FCSTD DOCUMENT  (FreeCAD 1.0R39319 (Git))
Label: Robot
License: All rights reserved
LicenseURL: https://en.wikipedia.org/wiki/All_rights_reserved
objects: App::Link×5, Spreadsheet::Sheet×1, Sketcher::SketchObject×1, PartDesign::Body×1
note: 3 computed .brp shape members not serialized (recipe doc carries the construction recipe); baked Part::Feature solids carry a one-line shape summary decoded from their .brp
EXTERNAL_REF file=DisplayHolder.FCStd obj=LinkGroup
EXTERNAL_REF file=RobotBody.FCStd obj=Body002
EXTERNAL_REF file=GT2_80.FCStd obj=LinkGroup
EXTERNAL_REF file=RobotBody.FCStd obj=LinkGroup
EXTERNAL_REF file=ChessBoard.FCStd obj=LinkGroup

FEATURE [Spreadsheet::Sheet] Spreadsheet  label="SpreadSheet"
  cells = A1='BaseWidth; B1(BaseWidth)=64; D1='TopThickness; E1(TopThickness)=2; G1='TeethNum; H1(TeethNum)=64; A2='BaseRectWidth; B2(BaseRectWidth)=40; D2='TopBearingHeight; E2(TopBearingHeight)=8; G2='CenterGearShaft; H2(CenterGearShaft)=0; A3='BaseRectHeight; B3(BaseRectHeight)=28; D3='TopBearingHole; E3(TopBearingHole)=25; G3='CutAngle; H3(CutAngle)=45; A4='HoleDiamter; B4(HoleDiamter)=28; D4='TopBearingDiameter; E4(TopBearingDiameter)=37; G4='ShaftDiameter; H4(ShaftDiameter)=6; A5='ScrewHoleDiamter; B5(ScrewHoleDiamter)=4.5; D5='TopThrustBearingHeight; E5(TopThrustBearingHeight)=4; G5='ShaftLength; H5(ShaftLength)=20; A6='CenterToScrewHole; B6(CenterToScrewHole)=24.5; D6='TopThrustBearingDiameter; E6(TopThrustBearingDiameter)=47; A7='Width; B7(Width)=120; D7='TopDiameter; E7(TopDiameter)=64; G7='GripperVerticalThread; H7(GripperVerticalThread)=5; A8='Length; B8(Length)=150; D8='TopFaceWidth; E8(TopFaceWidth)=50; G8='GripperVerticalBolt; H8(GripperVerticalBolt)=8; A9='Height; B9(Height)=70; D9='TopFaceSize; E9(TopFaceSize)=200; G9='GripperCenterToFork; H9(GripperCenterToFork)=10; A10='FirstLayerDepth; B10(FirstLayerDepth)=12; D10='SecondArmHeight; E10(SecondArmHeight)=37; G10='GripperForkDiameter; H10(GripperForkDiameter)=2; A11='UpperThickness; B11(UpperThickness)=5; D11='TopFaceHeight; E11(TopFaceHeight)=42; A12='UpperHeight; B12(UpperHeight)=80; D12='TopGearHoleDiameter; E12(TopGearHoleDiameter)=54; A13='StepperCenterToScewHole; B13(StepperCenterToScewHole)=15.5; D13='SecondShaftStepperHolderHeight; E13(SecondShaftStepperHolderHeight)=5; A14='ContactBaseWidth; B14(ContactBaseWidth)=10; D14='CenterToStepper; E14(CenterToStepper)=200; A15='StepperScrewHole; B15(StepperScrewHole)=3; D15='StepperSize; E15(StepperSize)=42; A16='MainShaftScrewBase; B16(MainShaftScrewBase)=11; D16='StepperHeight; E16(StepperHeight)=20; A17='MainShaftSize; B17(MainShaftSize)=60; D17='StepperMainHole; E17(StepperMainHole)=22; A18='MainShaftHolder; B18(MainShaftHolder)=23; D18='StepperCenterToScrew; E18(StepperCenterToScrew)=15.5; A19='MainShaftScrewDepth; B19(MainShaftScrewDepth)=5; D19='CuroaHoleSize; E19(CuroaHoleSize)=40; D20='ConnectMainArmHoleSpace; E20(ConnectMainArmHoleSpace)=5; A21='ContactHeight; B21(ContactHeight)=5; D21='SecondShaftScrewHole; E21(SecondShaftScrewHole)=4; A22='FirstArmHeight; B22(FirstArmHeight)=40; D22='SecondShaftThroughHole; E22(SecondShaftThroughHole)=8; A23='FirstArmInnerDiameter; B23(FirstArmInnerDiameter)=28; D23='BottomBearingInnerDiameter; E23(BottomBearingInnerDiameter)=40; A24='FirstArmInnerSpaceDiameter; B24(FirstArmInnerSpaceDiameter)=45; D24='BottomBearingOuterDiameter; E24(BottomBearingOuterDiameter)=52; A25='OuterDiameter; B25(OuterDiameter)=90; D25='BottomBearingHeight; E25(BottomBearingHeight)=7; A26='ContactArmWith; B26(ContactArmWith)=54; A27='ContactArmLength; B27(ContactArmLength)=15; A29='UpperBearingHole; B29(UpperBearingHole)=8; A30='UpperBearingInner; B30(UpperBearingInner)=6; A31='UpperBearingInnerDepth; B31(UpperBearingInnerDepth)=1; A32='UpperBearingOuter; B32(UpperBearingOuter)=8.1; A33='UpperBearingOuterDepth; B33(UpperBearingOuterDepth)=4; A34='LowerBearingHole; B34(LowerBearingHole)=10; A35='LowerBearingInner; B35(LowerBearingInner)=13.1; A36='LowerBearingInnerDepth; B36(LowerBearingInnerDepth)=1; A37='LowerBearingOuter; B37(LowerBearingOuter)=15.1; A38='LowerBearingOuterDepth; B38(LowerBearingOuterDepth)=4; A39='CenterSpace; B39(CenterSpace)=31; A40='UpperLowerSpace; B40(UpperLowerSpace)=13; A41='FirstToSecondHoleSpace; B41(FirstToSecondHoleSpace)=13; A42='GripperLowerBearingHole; B42(GripperLowerBearingHole)=8.1; A43='GripperUpperBearingHole; B43(GripperUpperBearingHole)=8.1; A44='GripperThickness; B44(GripperThickness)=1; A45='GripperLowerHoleDiameter; B45(GripperLowerHoleDiameter)=5; A46='GripperWidth; B46(GripperWidth)=44; A47='ThirdArmWidth; B47(ThirdArmWidth)=50; A48='ThirdArmLength; B48(ThirdArmLength)=100
FEATURE [App::Link] Link010  label="DisplayGroup"
  LinkPlacement = pos=(-57.6,-1.23143e-05,160.9) rot=(0,0,1;0rad)
  LinkedObject = -> <external DisplayHolder.FCStd>#LinkGroup
  Placement = pos=(-57.6,-1.23143e-05,160.9) rot=(0,0,1;0rad)
FEATURE [App::Link] Link011  label="BodyHolder001"
  LinkedObject = -> <external RobotBody.FCStd>#Body002
FEATURE [App::Link] Link012  label="SecondShaft"
  LinkPlacement = pos=(224.007,129.319,49) rot=(0,0,1;3.66519rad)
  LinkedObject = -> <external GT2_80.FCStd>#LinkGroup
  Placement = pos=(224.007,129.319,49) rot=(0,0,1;3.66519rad)
FEATURE [App::Link] Link013  label="RobotBody"
  LinkedObject = -> <external RobotBody.FCStd>#LinkGroup
FEATURE [App::Link] Link014  label="WoodenChessBoard"
  LinkPlacement = pos=(-58,223.8,-82.5) rot=(0,0,1;3.14159rad)
  LinkedObject = -> <external ChessBoard.FCStd>#LinkGroup
  Placement = pos=(-58,223.8,-82.5) rot=(0,0,1;3.14159rad)
FEATURE [Sketcher::SketchObject] Sketch
  ArcFitTolerance = 1e-06
  AttachmentSupport = -> [XY_Plane]
  FullyConstrained = true
  MakeInternals = false
  MapMode = 5
  sketch-geometry (2):
    g0: LineSegment StartX=0 StartY=0 StartZ=0 EndX=0 EndY=38.08 EndZ=0
    g1: LineSegment StartX=0 StartY=38.08 StartZ=0 EndX=-74.12 EndY=38.08 EndZ=0
  constraints (6):
    c: Coincident(g0,g-1)
    c: PointOnObject(g0,g-2)
    c: Coincident(g1,g0)
    c: Horizontal(g1)
    c: DistanceX(g1,g1) = 74.12
    c: DistanceY(g0,g0) = 38.08
FEATURE [PartDesign::Body] Body
  AllowCompound = false
  Group = -> [Sketch]
  Origin = -> Origin
  Placement = pos=(-0.1,-0.1,0) rot=(0,0,1;4.71239rad)

RESOLVED EXTERNAL PARTS (link-assembly join: the EXTERNAL_REF files above that resolve inside this repo's crawl, each included once):
---- part ChessBoard.FCStd = doc fcstd_d606b7bc8795 ----
FCSTD DOCUMENT  (FreeCAD 1.0R39319 (Git))
Label: ChessBoard
License: All rights reserved
LicenseURL: https://en.wikipedia.org/wiki/All_rights_reserved
objects: Sketcher::SketchObject×19, PartDesign::Pocket×10, PartDesign::Pad×8, PartDesign::Body×6, App::LinkGroup×3, App::Link×3, PartDesign::Hole×2, Part::Mirroring×2, Image::ImagePlane×1
note: 106 computed .brp shape members not serialized (recipe doc carries the construction recipe); baked Part::Feature solids carry a one-line shape summary decoded from their .brp
EXTERNAL_REF file=NavigationBoard.FCStd obj=LinkGroup
EXTERNAL_REF file=SnapLock.FCStd obj=LinkGroup
EXTERNAL_REF file=SnapLock.FCStd obj=LinkGroup001

FEATURE [Sketcher::SketchObject] Sketch
  ArcFitTolerance = 1e-06
  AttachmentSupport = -> [XY_Plane]
  FullyConstrained = true
  MakeInternals = false
  MapMode = 5
  sketch-geometry (5):
    g0: LineSegment StartX=-250 StartY=-150 StartZ=0 EndX=250 EndY=-150 EndZ=0
    g1: LineSegment StartX=250 StartY=-150 StartZ=0 EndX=250 EndY=150 EndZ=0
    g2: LineSegment StartX=250 StartY=150 StartZ=0 EndX=-250 EndY=150 EndZ=0
    g3: LineSegment StartX=-250 StartY=150 StartZ=0 EndX=-250 EndY=-150 EndZ=0
    g4: GeomPoint [constr] X=0 Y=0 Z=0
  constraints (12):
    c: Coincident(g0,g1)
    c: Coincident(g1,g2)
    c: Coincident(g2,g3)
    c: Coincident(g3,g0)
    c: Horizontal(g0)
    c: Horizontal(g2)
    c: Vertical(g1)
    c: Vertical(g3)
    c: Symmetric(g2,g0,g4)
    c: Distance(g1,g3) = 500
    c: Distance(g0,g2) = 300
    c: Coincident(g4,g-1)
FEATURE [Image::ImagePlane] ChessBoard
  Placement = pos=(0,0,30) rot=(0,0,1;0rad)
  XSize = 500.127
  YSize = 300.144
FEATURE [PartDesign::Pad] Pad
  Direction = (0,0,1)
  Length = 5
  Length2 = 10
  Profile = -> Sketch
  ReferenceAxis = -> Sketch [N_Axis]
  Refine = true
  Suppressed = false
  Type = 0
FEATURE [Sketcher::SketchObject] Sketch001
  ArcFitTolerance = 1e-06
  AttachmentSupport = -> [XY_Plane001]
  FullyConstrained = true
  MakeInternals = false
  MapMode = 5
  sketch-geometry (5):
    g0: LineSegment StartX=-150 StartY=-150 StartZ=0 EndX=150 EndY=-150 EndZ=0
    g1: LineSegment StartX=150 StartY=-150 StartZ=0 EndX=150 EndY=150 EndZ=0
    g2: LineSegment StartX=150 StartY=150 StartZ=0 EndX=-150 EndY=150 EndZ=0
    g3: LineSegment StartX=-150 StartY=150 StartZ=0 EndX=-150 EndY=-150 EndZ=0
    g4: GeomPoint [constr] X=0 Y=0 Z=0
  constraints (12):
    c: Coincident(g0,g1)
    c: Coincident(g1,g2)
    c: Coincident(g2,g3)
    c: Coincident(g3,g0)
    c: Horizontal(g0)
    c: Horizontal(g2)
    c: Vertical(g1)
    c: Vertical(g3)
    c: Symmetric(g2,g0,g4)
    c: Distance(g1,g3) = 300
    c: Distance(g0,g2) = 300
    c: Coincident(g4,g-1)
FEATURE [PartDesign::Pad] Pad001
  Direction = (0,0,1)
  Length = 5
  Length2 = 10
  Profile = -> Sketch001
  ReferenceAxis = -> Sketch001 [N_Axis]
  Refine = true
  Suppressed = false
  Type = 0
FEATURE [PartDesign::Body] Body001  label="MainBoard"
  AllowCompound = false
  Group = -> [Sketch001,Pad001]
  Origin = -> Origin001
  Placement = pos=(0,0,25) rot=(0,0,1;0rad)
  Tip = -> Pad001
FEATURE [Sketcher::SketchObject] Sketch002
  ArcFitTolerance = 1e-06
  AttachmentSupport = -> [XY_Plane002]
  FullyConstrained = true
  MakeInternals = false
  MapMode = 5
  sketch-geometry (4):
    g0: LineSegment StartX=0 StartY=0 StartZ=0 EndX=0 EndY=-300 EndZ=0
    g1: LineSegment StartX=0 StartY=-300 StartZ=0 EndX=100 EndY=-300 EndZ=0
    g2: LineSegment StartX=100 StartY=-300 StartZ=0 EndX=100 EndY=0 EndZ=0
    g3: LineSegment StartX=100 StartY=0 StartZ=0 EndX=0 EndY=0 EndZ=0
  constraints (11):
    c: Coincident(g0,g1)
    c: Coincident(g1,g2)
    c: Coincident(g2,g3)
    c: Coincident(g3,g0)
    c: Vertical(g0)
    c: Vertical(g2)
    c: Horizontal(g1)
    c: Horizontal(g3)
    c: Distance(g0,g2) = 100
    c: Distance(g1,g3) = 300
    c: Coincident(g0,g-1)
FEATURE [PartDesign::Pad] Pad002
  Direction = (0,0,1)
  Length = 5
  Length2 = 10
  Profile = -> Sketch002
  ReferenceAxis = -> Sketch002 [N_Axis]
  Refine = true
  Suppressed = false
  Type = 0
FEATURE [PartDesign::Body] Body002  label="DropLeft"
  AllowCompound = false
  Group = -> [Sketch002,Pad002]
  Origin = -> Origin002
  Placement = pos=(-250,150,25) rot=(0,0,1;0rad)
  Tip = -> Pad002
FEATURE [Sketcher::SketchObject] Sketch003
  ArcFitTolerance = 1e-06
  AttachmentSupport = -> [XY_Plane003]
  FullyConstrained = true
  MakeInternals = false
  MapMode = 5
  sketch-geometry (4):
    g0: LineSegment StartX=0 StartY=0 StartZ=0 EndX=-100 EndY=0 EndZ=0
    g1: LineSegment StartX=-100 StartY=0 StartZ=0 EndX=-100 EndY=-300 EndZ=0
    g2: LineSegment StartX=-100 StartY=-300 StartZ=0 EndX=0 EndY=-300 EndZ=0
    g3: LineSegment StartX=0 StartY=-300 StartZ=0 EndX=0 EndY=0 EndZ=0
  constraints (11):
    c: Coincident(g0,g1)
    c: Coincident(g1,g2)
    c: Coincident(g2,g3)
    c: Coincident(g3,g0)
    c: Horizontal(g0)
    c: Horizontal(g2)
    c: Vertical(g1)
    c: Vertical(g3)
    c: Distance(g1,g3) = 100
    c: Distance(g0,g2) = 300
    c: Coincident(g0,g-1)
FEATURE [PartDesign::Pad] Pad003
  Direction = (0,0,1)
  Length = 5
  Length2 = 10
  Profile = -> Sketch003
  ReferenceAxis = -> Sketch003 [N_Axis]
  Refine = true
  Suppressed = false
  Type = 0
FEATURE [PartDesign::Body] Body003  label="DropRight"
  AllowCompound = false
  Group = -> [Sketch003,Pad003]
  Origin = -> Origin003
  Placement = pos=(250,150,25) rot=(0,0,1;0rad)
  Tip = -> Pad003
FEATURE [Sketcher::SketchObject] Sketch004
  ArcFitTolerance = 1e-06
  AttachmentSupport = -> [XY_Plane004]
  FullyConstrained = false
  MakeInternals = false
  MapMode = 5
  sketch-geometry (13):
    g0: LineSegment StartX=0 StartY=40 StartZ=0 EndX=0 EndY=0 EndZ=0
    g1: LineSegment StartX=0 StartY=0 StartZ=0 EndX=160 EndY=0 EndZ=0
    g2: LineSegment StartX=0 StartY=40 StartZ=0 EndX=10 EndY=40 EndZ=0
    g3: LineSegment StartX=10 StartY=40 StartZ=0 EndX=10 EndY=30 EndZ=0
    g4: ArcOfCircle CenterX=30 CenterY=30 CenterZ=0 NormalX=0 NormalY=0 NormalZ=1 AngleXU=0 Radius=20 StartAngle=3.14159 EndAngle=4.71239
    g5: LineSegment StartX=90 StartY=42.0946 StartZ=0 EndX=115 EndY=42.0946 EndZ=0
    g6: LineSegment StartX=115 StartY=42.0946 StartZ=0 EndX=115 EndY=25 EndZ=0
    g7: LineSegment StartX=90 StartY=42.0946 StartZ=0 EndX=90 EndY=20 EndZ=0
    g8: LineSegment StartX=30 StartY=10 StartZ=0 EndX=80 EndY=10 EndZ=0
    g9: ArcOfCircle CenterX=125 CenterY=25 CenterZ=0 NormalX=0 NormalY=0 NormalZ=1 AngleXU=0 Radius=10 StartAngle=3.14159 EndAngle=4.71239
    g10: ArcOfCircle CenterX=80 CenterY=20 CenterZ=0 NormalX=0 NormalY=0 NormalZ=1 AngleXU=0 Radius=10 StartAngle=4.71239 EndAngle=6.28319
    g11: LineSegment StartX=125 StartY=15 StartZ=0 EndX=160 EndY=15 EndZ=0
    g12: LineSegment StartX=160 StartY=15 StartZ=0 EndX=160 EndY=0 EndZ=0
  constraints (38):
    c: PointOnObject(g0,g-2)
    c: Coincident(g0,g-1)
    c: Coincident(g0,g1)
    c: Coincident(g0,g2)
    c: Horizontal(g2)
    c: Coincident(g2,g3)
    c: Vertical(g3)
    c: Coincident(g4,g3)
    c: Vertical(g4,g4)
    c: Horizontal(g4,g3)
    c: Radius(g4) = 20
    c: DistanceY(g1,g9) = 15
    c: Distance(g2,g2) = 10
    c: DistanceY(g0,g0) = 40
    c: Horizontal(g5)
    c: Coincident(g5,g6)
    c: Vertical(g6)
    c: Coincident(g5,g7)
    c: Vertical(g7)
    c: Tangent(g4,g8) = -1.5708
    c: Coincident(g9,g6)
    c: Coincident(g10,g7)
    c: Coincident(g10,g8)
    c: Distance(g1,g8) = 10
    c: Radius(g10) = 10
    c: Vertical(g10,g8)
    c: Horizontal(g10,g7)
    c: Radius(g9) = 10
    c: Vertical(g9,g9)
    c: Horizontal(g9,g6)
    c: DistanceX(g-1,g10) = 80
    c: Tangent(g9,g11) = -1.5708
    c: Coincident(g11,g12)
    c: Vertical(g12)
    c: Coincident(g1,g12)
    c: Horizontal(g1)
    c: Distance(g-2,g12) = 160
    c: DistanceX(g5,g5) = 25
FEATURE [PartDesign::Pad] Pad004
  Direction = (0,0,1)
  Length = 29
  Length2 = 10
  Profile = -> Sketch004
  ReferenceAxis = -> Sketch004 [N_Axis]
  Refine = true
  Suppressed = false
  Type = 0
FEATURE [App::LinkGroup] LinkGroup002  label="TopBoard"
  ElementList = -> [Body001,Body002,Body003,ChessBoard]
  LinkMode = 0
  Placement = pos=(0,0,-1) rot=(0,0,1;0rad)
FEATURE [Sketcher::SketchObject] Sketch005
  ArcFitTolerance = 1e-06
  AttachmentSupport = -> [Pad]
  ExternalGeometry = -> [Sketch]
  FullyConstrained = false
  MakeInternals = false
  MapMode = 5
  Placement = pos=(0,0,0) rot=(1,0,0;3.14159rad)
  sketch-geometry (4):
    g0: LineSegment StartX=-92 StartY=-50 StartZ=0 EndX=-92 EndY=-193.39 EndZ=0
    g1: LineSegment StartX=-92 StartY=-193.39 StartZ=0 EndX=92 EndY=-193.39 EndZ=0
    g2: LineSegment StartX=92 StartY=-193.39 StartZ=0 EndX=92 EndY=-50 EndZ=0
    g3: LineSegment StartX=92 StartY=-50 StartZ=0 EndX=-92 EndY=-50 EndZ=0
  constraints (11):
    c: Coincident(g0,g1)
    c: Coincident(g1,g2)
    c: Coincident(g2,g3)
    c: Coincident(g3,g0)
    c: Vertical(g0)
    c: Vertical(g2)
    c: Horizontal(g1)
    c: Horizontal(g3)
    c: Distance(g-2,g2) = 92
    c: Distance(g-2,g0) = 92
    c: Distance(g-3,g3) = 100
FEATURE [PartDesign::Pocket] Pocket
  BaseFeature = -> Pad
  Direction = (0,0,1)
  Length = 5
  Length2 = 5
  Profile = -> Sketch005
  ReferenceAxis = -> Sketch005 [N_Axis]
  Refine = true
  Suppressed = false
  Type = 0
FEATURE [PartDesign::Body] Body  label="Bottom"
  AllowCompound = false
  Group = -> [Sketch,Pad,Sketch005,Pocket]
  Origin = -> Origin
  Tip = -> Pocket
FEATURE [Sketcher::SketchObject] Sketch006
  ArcFitTolerance = 1e-06
  AttachmentSupport = -> [Pad004]
  FullyConstrained = false
  MakeInternals = false
  MapMode = 5
  Placement = pos=(0,0,29) rot=(0,0,1;0rad)
  sketch-geometry (6):
    g0: LineSegment StartX=5 StartY=45 StartZ=0 EndX=5 EndY=5 EndZ=0
    g1: LineSegment StartX=5 StartY=5 StartZ=0 EndX=100 EndY=5 EndZ=0
    g2: LineSegment StartX=275.375 StartY=45 StartZ=0 EndX=5 EndY=45 EndZ=0
    g3: LineSegment StartX=100 StartY=5 StartZ=0 EndX=100 EndY=-8.02974 EndZ=0
    g4: LineSegment StartX=100 StartY=-8.02974 StartZ=0 EndX=275.375 EndY=-8.02974 EndZ=0
    g5: LineSegment StartX=275.375 StartY=45 StartZ=0 EndX=275.375 EndY=-8.02974 EndZ=0
  constraints (16):
    c: Coincident(g0,g1)
    c: Coincident(g2,g0)
    c: Vertical(g0)
    c: Horizontal(g1)
    c: Horizontal(g2)
    c: Distance(g-2,g0) = 5
    c: Distance(g-1,g1) = 5
    c: DistanceY(g0,g0) = 40
    c: Vertical(g3)
    c: Coincident(g3,g4)
    c: Horizontal(g4)
    c: Coincident(g1,g3)
    c: Coincident(g5,g2)
    c: Coincident(g5,g4)
    c: Vertical(g5)
    c: Distance(g-2,g3) = 100
FEATURE [PartDesign::Pocket] Pocket001
  BaseFeature = -> Pad004
  Direction = (0,0,-1)
  Length = 5
  Length2 = 5
  Profile = -> Sketch006
  ReferenceAxis = -> Sketch006 [N_Axis]
  Refine = true
  Suppressed = false
  Type = 0
FEATURE [Sketcher::SketchObject] Sketch007
  ArcFitTolerance = 1e-06
  AttachmentSupport = -> [Pocket001]
  FullyConstrained = false
  MakeInternals = false
  MapMode = 5
  Placement = pos=(0,0,0) rot=(1,0,0;3.14159rad)
  sketch-geometry (6):
    g0: LineSegment StartX=5 StartY=-5 StartZ=0 EndX=5 EndY=-45 EndZ=0
    g1: LineSegment StartX=5 StartY=-45 StartZ=0 EndX=160 EndY=-45 EndZ=0
    g2: LineSegment StartX=45 StartY=-5 StartZ=0 EndX=5 EndY=-5 EndZ=0
    g3: LineSegment StartX=45 StartY=-5 StartZ=0 EndX=45 EndY=8.54607 EndZ=0
    g4: LineSegment StartX=45 StartY=8.54607 StartZ=0 EndX=160 EndY=8.54607 EndZ=0
    g5: LineSegment StartX=160 StartY=8.54607 StartZ=0 EndX=160 EndY=-45 EndZ=0
  constraints (17):
    c: Coincident(g0,g1)
    c: Coincident(g2,g0)
    c: Vertical(g0)
    c: Horizontal(g1)
    c: Horizontal(g2)
    c: Distance(g-1,g2) = 5
    c: Distance(g-2,g0) = 5
    c: DistanceY(g0,g0) = 40
    c: Coincident(g2,g3)
    c: Vertical(g3)
    c: Coincident(g3,g4)
    c: Horizontal(g4)
    c: Coincident(g4,g5)
    c: Coincident(g5,g1)
    c: Vertical(g5)
    c: DistanceX(g0,g2) = 40
    c: Distance(g1,g-2) = 160
FEATURE [PartDesign::Pocket] Pocket002
  BaseFeature = -> Pocket001
  Direction = (0,0,1)
  Length = 5
  Length2 = 5
  Profile = -> Sketch007
  ReferenceAxis = -> Sketch007 [N_Axis]
  Refine = true
  Suppressed = false
  Type = 0
FEATURE [Sketcher::SketchObject] Sketch008
  ArcFitTolerance = 1e-06
  AttachmentSupport = -> [Pocket002]
  ExternalGeometry = -> [Pocket002]
  FullyConstrained = true
  MakeInternals = false
  MapMode = 5
  Placement = pos=(0,0,24) rot=(0,0,1;0rad)
  sketch-geometry (1):
    g0: Circle CenterX=110 CenterY=10 CenterZ=0 NormalX=0 NormalY=0 NormalZ=1 AngleXU=0 Radius=5
  constraints (3):
    c: Diameter(g0) = 10
    c: Distance(g0,g-1) = 10
    c: DistanceX(g-3,g0) = 10
FEATURE [PartDesign::Pocket] Pocket003
  BaseFeature = -> Pocket002
  Direction = (0,0,-1)
  Length = 10
  Length2 = 5
  Profile = -> Sketch008
  ReferenceAxis = -> Sketch008 [N_Axis]
  Refine = true
  Suppressed = false
  Type = 0
FEATURE [Sketcher::SketchObject] Sketch009
  ArcFitTolerance = 1e-06
  AttachmentSupport = -> [XY_Plane005]
  FullyConstrained = false
  MakeInternals = false
  MapMode = 5
  sketch-geometry (13):
    g0: LineSegment StartX=0 StartY=40 StartZ=0 EndX=0 EndY=0 EndZ=0
    g1: LineSegment StartX=0 StartY=0 StartZ=0 EndX=160 EndY=0 EndZ=0
    g2: LineSegment StartX=0 StartY=40 StartZ=0 EndX=10 EndY=40 EndZ=0
    g3: LineSegment StartX=10 StartY=40 StartZ=0 EndX=10 EndY=30 EndZ=0
    g4: ArcOfCircle CenterX=30 CenterY=30 CenterZ=0 NormalX=0 NormalY=0 NormalZ=1 AngleXU=0 Radius=20 StartAngle=3.14159 EndAngle=4.71239
    g5: LineSegment StartX=90 StartY=42.0946 StartZ=0 EndX=115 EndY=42.0946 EndZ=0
    g6: LineSegment StartX=115 StartY=42.0946 StartZ=0 EndX=115 EndY=25 EndZ=0
    g7: LineSegment StartX=90 StartY=42.0946 StartZ=0 EndX=90 EndY=20 EndZ=0
    g8: LineSegment StartX=30 StartY=10 StartZ=0 EndX=80 EndY=10 EndZ=0
    g9: ArcOfCircle CenterX=125 CenterY=25 CenterZ=0 NormalX=0 NormalY=0 NormalZ=1 AngleXU=0 Radius=10 StartAngle=3.14159 EndAngle=4.71239
    g10: ArcOfCircle CenterX=80 CenterY=20 CenterZ=0 NormalX=0 NormalY=0 NormalZ=1 AngleXU=0 Radius=10 StartAngle=4.71239 EndAngle=6.28319
    g11: LineSegment StartX=125 StartY=15 StartZ=0 EndX=160 EndY=15 EndZ=0
    g12: LineSegment StartX=160 StartY=15 StartZ=0 EndX=160 EndY=0 EndZ=0
  constraints (38):
    c: PointOnObject(g0,g-2)
    c: Coincident(g0,g-1)
    c: Coincident(g0,g1)
    c: Coincident(g0,g2)
    c: Horizontal(g2)
    c: Coincident(g2,g3)
    c: Vertical(g3)
    c: Coincident(g4,g3)
    c: Vertical(g4,g4)
    c: Horizontal(g4,g3)
    c: Radius(g4) = 20
    c: DistanceY(g1,g9) = 15
    c: Distance(g2,g2) = 10
    c: DistanceY(g0,g0) = 40
    c: Horizontal(g5)
    c: Coincident(g5,g6)
    c: Vertical(g6)
    c: Coincident(g5,g7)
    c: Vertical(g7)
    c: Tangent(g4,g8) = -1.5708
    c: Coincident(g9,g6)
    c: Coincident(g10,g7)
    c: Coincident(g10,g8)
    c: Distance(g1,g8) = 10
    c: Radius(g10) = 10
    c: Vertical(g10,g8)
    c: Horizontal(g10,g7)
    c: Radius(g9) = 10
    c: Vertical(g9,g9)
    c: Horizontal(g9,g6)
    c: DistanceX(g-1,g10) = 80
    c: Tangent(g9,g11) = -1.5708
    c: Coincident(g11,g12)
    c: Vertical(g12)
    c: Coincident(g1,g12)
    c: Horizontal(g1)
    c: Distance(g-2,g12) = 160
    c: DistanceX(g5,g5) = 25
FEATURE [PartDesign::Pad] Pad005
  Direction = (0,0,1)
  Length = 29
  Length2 = 10
  Profile = -> Sketch009
  ReferenceAxis = -> Sketch009 [N_Axis]
  Refine = true
  Suppressed = false
  Type = 0
FEATURE [Sketcher::SketchObject] Sketch010
  ArcFitTolerance = 1e-06
  AttachmentSupport = -> [Pad005]
  FullyConstrained = false
  MakeInternals = false
  MapMode = 5
  Placement = pos=(0,0,29) rot=(0,0,1;0rad)
  sketch-geometry (6):
    g0: LineSegment StartX=5 StartY=45 StartZ=0 EndX=5 EndY=5 EndZ=0
    g1: LineSegment StartX=5 StartY=5 StartZ=0 EndX=100 EndY=5 EndZ=0
    g2: LineSegment StartX=275.375 StartY=45 StartZ=0 EndX=5 EndY=45 EndZ=0
    g3: LineSegment StartX=100 StartY=5 StartZ=0 EndX=100 EndY=-8.02974 EndZ=0
    g4: LineSegment StartX=100 StartY=-8.02974 StartZ=0 EndX=275.375 EndY=-8.02974 EndZ=0
    g5: LineSegment StartX=275.375 StartY=45 StartZ=0 EndX=275.375 EndY=-8.02974 EndZ=0
  constraints (16):
    c: Coincident(g0,g1)
    c: Coincident(g2,g0)
    c: Vertical(g0)
    c: Horizontal(g1)
    c: Horizontal(g2)
    c: Distance(g-2,g0) = 5
    c: Distance(g-1,g1) = 5
    c: DistanceY(g0,g0) = 40
    c: Vertical(g3)
    c: Coincident(g3,g4)
    c: Horizontal(g4)
    c: Coincident(g1,g3)
    c: Coincident(g5,g2)
    c: Coincident(g5,g4)
    c: Vertical(g5)
    c: Distance(g-2,g3) = 100
FEATURE [PartDesign::Pocket] Pocket004
  BaseFeature = -> Pad005
  Direction = (0,0,-1)
  Length = 5
  Length2 = 5
  Profile = -> Sketch010
  ReferenceAxis = -> Sketch010 [N_Axis]
  Refine = true
  Suppressed = false
  Type = 0
FEATURE [Sketcher::SketchObject] Sketch011
  ArcFitTolerance = 1e-06
  AttachmentSupport = -> [Pocket004]
  FullyConstrained = false
  MakeInternals = false
  MapMode = 5
  Placement = pos=(0,0,0) rot=(1,0,0;3.14159rad)
  sketch-geometry (6):
    g0: LineSegment StartX=5 StartY=-5 StartZ=0 EndX=5 EndY=-45 EndZ=0
    g1: LineSegment StartX=5 StartY=-45 StartZ=0 EndX=160 EndY=-45 EndZ=0
    g2: LineSegment StartX=45 StartY=-5 StartZ=0 EndX=5 EndY=-5 EndZ=0
    g3: LineSegment StartX=45 StartY=-5 StartZ=0 EndX=45 EndY=8.54607 EndZ=0
    g4: LineSegment StartX=45 StartY=8.54607 StartZ=0 EndX=160 EndY=8.54607 EndZ=0
    g5: LineSegment StartX=160 StartY=8.54607 StartZ=0 EndX=160 EndY=-45 EndZ=0
  constraints (17):
    c: Coincident(g0,g1)
    c: Coincident(g2,g0)
    c: Vertical(g0)
    c: Horizontal(g1)
    c: Horizontal(g2)
    c: Distance(g-1,g2) = 5
    c: Distance(g-2,g0) = 5
    c: DistanceY(g0,g0) = 40
    c: Coincident(g2,g3)
    c: Vertical(g3)
    c: Coincident(g3,g4)
    c: Horizontal(g4)
    c: Coincident(g4,g5)
    c: Coincident(g5,g1)
    c: Vertical(g5)
    c: DistanceX(g0,g2) = 40
    c: Distance(g1,g-2) = 160
FEATURE [PartDesign::Pocket] Pocket005
  BaseFeature = -> Pocket004
  Direction = (0,0,1)
  Length = 5
  Length2 = 5
  Profile = -> Sketch011
  ReferenceAxis = -> Sketch011 [N_Axis]
  Refine = true
  Suppressed = false
  Type = 0
FEATURE [Sketcher::SketchObject] Sketch012
  ArcFitTolerance = 1e-06
  AttachmentSupport = -> [Pocket005]
  ExternalGeometry = -> [Pocket005]
  FullyConstrained = true
  MakeInternals = false
  MapMode = 5
  Placement = pos=(0,0,24) rot=(0,0,1;0rad)
  sketch-geometry (1):
    g0: Circle CenterX=110 CenterY=10 CenterZ=0 NormalX=0 NormalY=0 NormalZ=1 AngleXU=0 Radius=5
  constraints (3):
    c: Diameter(g0) = 10
    c: Distance(g0,g-1) = 10
    c: DistanceX(g-3,g0) = 10
FEATURE [PartDesign::Pocket] Pocket006
  BaseFeature = -> Pocket005
  Direction = (0,0,-1)
  Length = 10
  Length2 = 5
  Profile = -> Sketch012
  ReferenceAxis = -> Sketch012 [N_Axis]
  Refine = true
  Suppressed = false
  Type = 0
FEATURE [Sketcher::SketchObject] Sketch013
  ArcFitTolerance = 1e-06
  AttachmentSupport = -> [Pocket006]
  ExternalGeometry = -> [Pocket006]
  FullyConstrained = true
  MakeInternals = false
  MapMode = 5
  Placement = pos=(160,0,0) rot=(0.57735,0.57735,0.57735;2.0944rad)
  sketch-geometry (4):
    g0: LineSegment StartX=15 StartY=24 StartZ=0 EndX=0 EndY=24 EndZ=0
    g1: LineSegment StartX=0 StartY=24 StartZ=0 EndX=0 EndY=15 EndZ=0
    g2: LineSegment StartX=0 StartY=15 StartZ=0 EndX=15 EndY=15 EndZ=0
    g3: LineSegment StartX=15 StartY=15 StartZ=0 EndX=15 EndY=24 EndZ=0
  constraints (11):
    c: Coincident(g0,g1)
    c: Coincident(g1,g2)
    c: Coincident(g2,g3)
    c: Coincident(g3,g0)
    c: Horizontal(g0)
    c: Horizontal(g2)
    c: Vertical(g1)
    c: Vertical(g3)
    c: Coincident(g0,g-3)
    c: PointOnObject(g1,g-2)
    c: Distance(g-1,g2) = 15
FEATURE [PartDesign::Pad] Pad006
  BaseFeature = -> Pocket006
  Direction = (1,0,0)
  Length = 15
  Length2 = 10
  Profile = -> Sketch013
  ReferenceAxis = -> Sketch013 [N_Axis]
  Refine = true
  Suppressed = false
  Type = 0
FEATURE [Sketcher::SketchObject] Sketch014
  ArcFitTolerance = 1e-06
  AttachmentSupport = -> [Pad006]
  ExternalGeometry = -> [Pad006]
  FullyConstrained = true
  MakeInternals = false
  MapMode = 5
  Placement = pos=(0,0,24) rot=(0,0,1;0rad)
  sketch-geometry (1):
    g0: Circle CenterX=167.5 CenterY=7.5 CenterZ=0 NormalX=0 NormalY=0 NormalZ=1 AngleXU=0 Radius=1.75
  constraints (2):
    c: Diameter(g0) = 3.5
    c: Symmetric(g-3,g-4,g0)
FEATURE [PartDesign::Hole] Hole
  BaseFeature = -> Pad006
  CustomThreadClearance = 0
  Depth = 25
  DepthType = 0
  Diameter = 3
  DrillForDepth = false
  DrillPoint = 1
  DrillPointAngle = 118
  HoleCutCountersinkAngle = 90
  HoleCutCustomValues = false
  HoleCutDepth = 0
  HoleCutDiameter = 6.1
  HoleCutType = 0
  ModelThread = false
  Profile = -> Sketch014
  Refine = true
  Suppressed = false
  Tapered = false
  TaperedAngle = 90
  ThreadClass = 0
  ThreadDepth = 25
  ThreadDepthType = 0
  ThreadDirection = 0
  ThreadFit = 0
  ThreadSize = 0
  ThreadType = 0
  Threaded = false
  UseCustomThreadClearance = false
FEATURE [PartDesign::Hole] Hole001
  BaseFeature = -> Hole
  CustomThreadClearance = 0
  Depth = 6
  DepthType = 0
  Diameter = 8
  DrillForDepth = false
  DrillPoint = 0
  DrillPointAngle = 118
  HoleCutCountersinkAngle = 90
  HoleCutCustomValues = false
  HoleCutDepth = 0
  HoleCutDiameter = 6.1
  HoleCutType = 0
  ModelThread = false
  Profile = -> Sketch014
  Refine = true
  Suppressed = false
  Tapered = false
  TaperedAngle = 90
  ThreadClass = 0
  ThreadDepth = 6
  ThreadDepthType = 0
  ThreadDirection = 0
  ThreadFit = 0
  ThreadSize = 0
  ThreadType = 0
  Threaded = false
  UseCustomThreadClearance = false
FEATURE [App::Link] Link  label="NavigationBoard"
  LinkPlacement = pos=(200.5,-84.6001,14) rot=(0,0,1;0rad)
  LinkedObject = -> <external NavigationBoard.FCStd>#LinkGroup
  Placement = pos=(200.5,-84.6001,14) rot=(0,0,1;0rad)
FEATURE [Sketcher::SketchObject] Sketch015
  ArcFitTolerance = 1e-06
  AttachmentSupport = -> [Pocket003]
  ExternalGeometry = -> [Pocket003]
  FullyConstrained = true
  MakeInternals = false
  MapMode = 5
  Placement = pos=(0,0,24) rot=(0,0,1;0rad)
  sketch-geometry (6):
    g0: Circle CenterX=11 CenterY=11 CenterZ=0 NormalX=0 NormalY=0 NormalZ=1 AngleXU=0 Radius=2
    g1: Circle CenterX=94 CenterY=11 CenterZ=0 NormalX=0 NormalY=0 NormalZ=1 AngleXU=0 Radius=2
    g2: Circle CenterX=94 CenterY=36 CenterZ=0 NormalX=0 NormalY=0 NormalZ=1 AngleXU=0 Radius=2
    g3: Circle CenterX=106 CenterY=36 CenterZ=0 NormalX=0 NormalY=0 NormalZ=1 AngleXU=0 Radius=2
    g4: Circle CenterX=124 CenterY=6 CenterZ=0 NormalX=0 NormalY=0 NormalZ=1 AngleXU=0 Radius=2
    g5: Circle CenterX=154 CenterY=6 CenterZ=0 NormalX=0 NormalY=0 NormalZ=1 AngleXU=0 Radius=2
  constraints (18):
    c: Diameter(g0) = 4
    c: Diameter(g1) = 4
    c: Diameter(g2) = 4
    c: Distance(g1,g-3) = 6
    c: Vertical(g2,g1)
    c: Distance(g1,g-5) = 6
    c: DistanceY(g1,g2) = 25
    c: Distance(g0,g-5) = 6
    c: Distance(g0,g-4) = 6
    c: Diameter(g3) = 4
    c: Diameter(g4) = 4
    c: Horizontal(g3,g2)
    c: Distance(g3,g-3) = 6
    c: Distance(g4,g-1) = 6
    c: Distance(g4,g-3) = 24
    c: Diameter(g5) = 4
    c: Distance(g5,g-1) = 6
    c: Distance(g5,g-6) = 6
FEATURE [PartDesign::Pocket] Pocket007
  BaseFeature = -> Pocket003
  Direction = (0,0,-1)
  Length = 5
  Length2 = 5
  Profile = -> Sketch015
  ReferenceAxis = -> Sketch015 [N_Axis]
  Refine = true
  Suppressed = false
  Type = 1
FEATURE [PartDesign::Body] Body004  label="AnchorBL"
  AllowCompound = false
  Group = -> [Sketch004,Pad004,Sketch006,Pocket001,Sketch007,Pocket002,Sketch008,Pocket003,Sketch015,Pocket007]
  Origin = -> Origin004
  Placement = pos=(-250,-150,0) rot=(0,0,1;0rad)
  Tip = -> Pocket007
FEATURE [Part::Mirroring] Part__Mirroring001  label="AnchorBR"
  Base = (0,0,0)
  Normal = (1,0,0)
  Source = -> Body004
FEATURE [Sketcher::SketchObject] Sketch016
  ArcFitTolerance = 1e-06
  AttachmentSupport = -> [Hole001]
  ExternalGeometry = -> [Hole001]
  FullyConstrained = true
  MakeInternals = false
  MapMode = 5
  Placement = pos=(0,0,24) rot=(0,0,1;0rad)
  sketch-geometry (6):
    g0: Circle CenterX=11 CenterY=11 CenterZ=0 NormalX=0 NormalY=0 NormalZ=1 AngleXU=0 Radius=2
    g1: Circle CenterX=94 CenterY=11 CenterZ=0 NormalX=0 NormalY=0 NormalZ=1 AngleXU=0 Radius=2
    g2: Circle CenterX=94 CenterY=36 CenterZ=0 NormalX=0 NormalY=0 NormalZ=1 AngleXU=0 Radius=2
    g3: Circle CenterX=106 CenterY=36 CenterZ=0 NormalX=0 NormalY=0 NormalZ=1 AngleXU=0 Radius=2
    g4: Circle CenterX=124 CenterY=6 CenterZ=0 NormalX=0 NormalY=0 NormalZ=1 AngleXU=0 Radius=2
    g5: Circle CenterX=152 CenterY=6 CenterZ=0 NormalX=0 NormalY=0 NormalZ=1 AngleXU=0 Radius=2
  constraints (18):
    c: Diameter(g0) = 4
    c: Diameter(g1) = 4
    c: Diameter(g2) = 4
    c: Diameter(g3) = 4
    c: Diameter(g4) = 4
    c: Diameter(g5) = 4
    c: Distance(g0,g-3) = 6
    c: Distance(g0,g-4) = 6
    c: DistanceX(g1,g-4) = 6
    c: Distance(g1,g-4) = 6
    c: Vertical(g1,g2)
    c: Horizontal(g3,g2)
    c: DistanceX(g-4,g3) = 6
    c: Distance(g4,g-1) = 6
    c: DistanceX(g-4,g4) = 24
    c: Horizontal(g5,g4)
    c: Distance(g5,g-5) = 8
    c: DistanceY(g1,g2) = 25
FEATURE [PartDesign::Pocket] Pocket008
  BaseFeature = -> Hole001
  Direction = (0,0,-1)
  Length = 5
  Length2 = 5
  Profile = -> Sketch016
  ReferenceAxis = -> Sketch016 [N_Axis]
  Refine = true
  Suppressed = false
  Type = 1
FEATURE [App::Link] Link001  label="LatchesLock"
  LinkPlacement = pos=(100,171,7.49998) rot=(0,1,0;1.5708rad)
  LinkedObject = -> <external SnapLock.FCStd>#LinkGroup
  Placement = pos=(100,171,7.49998) rot=(0,1,0;1.5708rad)
FEATURE [Sketcher::SketchObject] Sketch017
  ArcFitTolerance = 1e-06
  AttachmentSupport = -> [Pocket008]
  ExternalGeometry = -> [Pocket008]
  FullyConstrained = true
  MakeInternals = false
  MapMode = 5
  Placement = pos=(0,0,24) rot=(0,0,1;0rad)
  sketch-geometry (4):
    g0: LineSegment StartX=146 StartY=0 StartZ=0 EndX=146 EndY=-13 EndZ=0
    g1: ArcOfCircle CenterX=150 CenterY=-13 CenterZ=0 NormalX=0 NormalY=0 NormalZ=1 AngleXU=0 Radius=4 StartAngle=3.14159 EndAngle=6.28319
    g2: LineSegment StartX=154 StartY=-13 StartZ=0 EndX=154 EndY=0 EndZ=0
    g3: LineSegment StartX=146 StartY=0 StartZ=0 EndX=154 EndY=0 EndZ=0
  constraints (12):
    c: Vertical(g0)
    c: Coincident(g1,g0)
    c: Radius(g1) = 4
    c: Tangent(g1,g2) = -1.5708
    c: Vertical(g2)
    c: Coincident(g0,g3)
    c: Coincident(g3,g2)
    c: DistanceY(g1,g-1) = 13
    c: Symmetric(g0,g1,g1)
    c: Distance(g2,g-3) = 6
    c: Horizontal(g3)
    c: Horizontal(g2,g-3)
FEATURE [PartDesign::Pad] Pad007
  BaseFeature = -> Pocket008
  Direction = (0,0,1)
  Length = 24
  Length2 = 10
  Profile = -> Sketch017
  ReferenceAxis = -> Sketch017 [N_Axis]
  Refine = true
  Reversed = true
  Suppressed = false
  Type = 0
FEATURE [Sketcher::SketchObject] Sketch018
  ArcFitTolerance = 1e-06
  AttachmentSupport = -> [Pad007]
  FullyConstrained = true
  MakeInternals = false
  MapMode = 5
  Placement = pos=(154,0,0) rot=(0.57735,0.57735,0.57735;2.0944rad)
  sketch-geometry (4):
    g0: LineSegment StartX=0 StartY=15 StartZ=0 EndX=-8 EndY=15 EndZ=0
    g1: LineSegment StartX=-8 StartY=15 StartZ=0 EndX=-8 EndY=5 EndZ=0
    g2: LineSegment StartX=-8 StartY=5 StartZ=0 EndX=0 EndY=5 EndZ=0
    g3: LineSegment StartX=0 StartY=5 StartZ=0 EndX=0 EndY=15 EndZ=0
  constraints (12):
    c: Coincident(g0,g1)
    c: Coincident(g1,g2)
    c: Coincident(g2,g3)
    c: Coincident(g3,g0)
    c: Horizontal(g0)
    c: Horizontal(g2)
    c: Vertical(g1)
    c: Vertical(g3)
    c: Distance(g1,g3) = 8
    c: Distance(g0,g2) = 10
    c: PointOnObject(g0,g-2)
    c: Distance(g-1,g2) = 5
FEATURE [PartDesign::Pocket] Pocket009
  BaseFeature = -> Pad007
  Direction = (-1,0,0)
  Length = 8
  Length2 = 5
  Profile = -> Sketch018
  ReferenceAxis = -> Sketch018 [N_Axis]
  Refine = true
  Suppressed = false
  Type = 0
FEATURE [PartDesign::Body] Body005  label="AnchorTR"
  AllowCompound = false
  Group = -> [Sketch009,Pad005,Sketch010,Pocket004,Sketch011,Pocket005,Sketch012,Pocket006,Sketch013,Pad006,Sketch014,Hole,Hole001,Sketch016,Pocket008,Sketch017,Pad007,Sketch018,Pocket009]
  Origin = -> Origin005
  Placement = pos=(250,150,0) rot=(0,0,1;3.14159rad)
  Tip = -> Pocket009
FEATURE [Part::Mirroring] Part__Mirroring  label="AnchorTL"
  Base = (0,0,0)
  Normal = (1,0,0)
  Source = -> Body005
FEATURE [App::LinkGroup] LinkGroup001  label="Anchors"
  ElementList = -> [Body004,Part__Mirroring001,Body005,Part__Mirroring]
  LinkMode = 0
  Placement = pos=(0,4.76837e-08,9.53674e-07) rot=(0,0,1;0rad)
FEATURE [App::LinkGroup] LinkGroup  label="WoodenChessBoard"
  ElementList = -> [Body,LinkGroup001,LinkGroup002,Link]
  LinkMode = 0
FEATURE [App::Link] Link002  label="LatchesLockRight"
  LinkPlacement = pos=(-100,171,7.5) rot=(0,1,0;1.5708rad)
  LinkedObject = -> <external SnapLock.FCStd>#LinkGroup001
  Placement = pos=(-100,171,7.5) rot=(0,1,0;1.5708rad)
---- part DisplayHolder.FCStd = doc fcstd_62bf7a6708b3 ----
FCSTD DOCUMENT  (FreeCAD 1.0R39319 (Git))
Label: DisplayHolder
License: All rights reserved
LicenseURL: https://en.wikipedia.org/wiki/All_rights_reserved
objects: Sketcher::SketchObject×13, PartDesign::Pad×7, PartDesign::Pocket×6, PartDesign::Body×4, PartDesign::Fillet×2, PartDesign::Mirrored×1, PartDesign::Hole×1, App::LinkGroup×1
note: 80 computed .brp shape members not serialized (recipe doc carries the construction recipe); baked Part::Feature solids carry a one-line shape summary decoded from their .brp

FEATURE [Sketcher::SketchObject] Sketch
  ArcFitTolerance = 1e-06
  AttachmentSupport = -> [XZ_Plane]
  FullyConstrained = true
  MakeInternals = false
  MapMode = 5
  Placement = pos=(0,0,0) rot=(1,0,0;1.5708rad)
  sketch-geometry (5):
    g0: LineSegment StartX=-75 StartY=-48.5 StartZ=0 EndX=75 EndY=-48.5 EndZ=0
    g1: LineSegment StartX=75 StartY=-48.5 StartZ=0 EndX=75 EndY=48.5 EndZ=0
    g2: LineSegment StartX=75 StartY=48.5 StartZ=0 EndX=-75 EndY=48.5 EndZ=0
    g3: LineSegment StartX=-75 StartY=48.5 StartZ=0 EndX=-75 EndY=-48.5 EndZ=0
    g4: GeomPoint [constr] X=0 Y=0 Z=0
  constraints (12):
    c: Coincident(g0,g1)
    c: Coincident(g1,g2)
    c: Coincident(g2,g3)
    c: Coincident(g3,g0)
    c: Horizontal(g0)
    c: Horizontal(g2)
    c: Vertical(g1)
    c: Vertical(g3)
    c: Symmetric(g2,g0,g4)
    c: Distance(g1,g3) = 150
    c: Distance(g0,g2) = 97
    c: Coincident(g4,g-1)
FEATURE [PartDesign::Pad] Pad
  Direction = (0,-1,2e-16)
  Length = 15
  Length2 = 10
  Placement = pos=(0,0,0) rot=(1,0,0;1.5708rad)
  Profile = -> Sketch
  ReferenceAxis = -> Sketch [N_Axis]
  Refine = true
  Suppressed = false
  Type = 0
FEATURE [Sketcher::SketchObject] Sketch001
  ArcFitTolerance = 1e-06
  AttachmentSupport = -> [Pad]
  FullyConstrained = true
  MakeInternals = false
  MapMode = 5
  Placement = pos=(0,-15,0) rot=(1,0,0;1.5708rad)
  sketch-geometry (5):
    g0: LineSegment StartX=-61 StartY=-39 StartZ=0 EndX=61 EndY=-39 EndZ=0
    g1: LineSegment StartX=61 StartY=-39 StartZ=0 EndX=61 EndY=39 EndZ=0
    g2: LineSegment StartX=61 StartY=39 StartZ=0 EndX=-61 EndY=39 EndZ=0
    g3: LineSegment StartX=-61 StartY=39 StartZ=0 EndX=-61 EndY=-39 EndZ=0
    g4: GeomPoint [constr] X=0 Y=0 Z=0
  constraints (12):
    c: Coincident(g0,g1)
    c: Coincident(g1,g2)
    c: Coincident(g2,g3)
    c: Coincident(g3,g0)
    c: Horizontal(g0)
    c: Horizontal(g2)
    c: Vertical(g1)
    c: Vertical(g3)
    c: Symmetric(g2,g0,g4)
    c: Distance(g1,g3) = 122
    c: Distance(g0,g2) = 78
    c: Coincident(g4,g-1)
FEATURE [PartDesign::Pocket] Pocket
  BaseFeature = -> Pad
  Direction = (0,1,-2e-16)
  Length = 10
  Length2 = 5
  Placement = pos=(0,0,0) rot=(1,0,0;1.5708rad)
  Profile = -> Sketch001
  ReferenceAxis = -> Sketch001 [N_Axis]
  Refine = true
  Suppressed = false
  Type = 0
FEATURE [Sketcher::SketchObject] Sketch002
  ArcFitTolerance = 1e-06
  AttachmentSupport = -> [Pocket]
  FullyConstrained = false
  MakeInternals = false
  MapMode = 5
  Placement = pos=(0,0,0) rot=(-1,0,0;1.5708rad)
  sketch-geometry (4):
    g0: LineSegment StartX=-57.9918 StartY=37 StartZ=0 EndX=58 EndY=37 EndZ=0
    g1: LineSegment StartX=58 StartY=37 StartZ=0 EndX=58 EndY=-33 EndZ=0
    g2: LineSegment StartX=-57.9918 StartY=-33 StartZ=0 EndX=-57.9918 EndY=37 EndZ=0
    g3: LineSegment StartX=-57.9918 StartY=-33 StartZ=0 EndX=58 EndY=-33 EndZ=0
  constraints (10):
    c: Horizontal(g0)
    c: Distance(g-1,g0) = 37
    c: Coincident(g0,g2)
    c: Coincident(g0,g1)
    c: Distance(g-1,g3) = 33
    c: Coincident(g2,g3)
    c: Coincident(g1,g3)
    c: Horizontal(g3)
    c: Vertical(g2)
    c: Vertical(g1)
FEATURE [PartDesign::Pocket] Pocket001
  BaseFeature = -> Pocket
  Direction = (0,-1,-2e-16)
  Length = 5
  Length2 = 5
  Placement = pos=(0,0,0) rot=(1,0,0;1.5708rad)
  Profile = -> Sketch002
  ReferenceAxis = -> Sketch002 [N_Axis]
  Refine = true
  Suppressed = false
  Type = 0
FEATURE [Sketcher::SketchObject] Sketch003
  ArcFitTolerance = 1e-06
  AttachmentSupport = -> [Pocket001]
  ExternalGeometry = -> [Pocket001]
  FullyConstrained = false
  MakeInternals = false
  MapMode = 5
  Placement = pos=(0,-15,0) rot=(1,0,0;1.5708rad)
  sketch-geometry (8):
    g0: LineSegment StartX=-45 StartY=48.5 StartZ=0 EndX=-60 EndY=48.5 EndZ=0
    g1: LineSegment StartX=-60 StartY=48.5 StartZ=0 EndX=-75 EndY=13 EndZ=0
    g2: LineSegment StartX=-75 StartY=13 StartZ=0 EndX=-75 EndY=-13 EndZ=0
    g3: LineSegment StartX=-75 StartY=-13 StartZ=0 EndX=-60 EndY=-48.5 EndZ=0
    g4: LineSegment StartX=-60 StartY=-48.5 StartZ=0 EndX=-25 EndY=-48.5 EndZ=0
    g5: LineSegment StartX=-45 StartY=48.5 StartZ=0 EndX=-45 EndY=-25.4373 EndZ=0
    g6: LineSegment StartX=-45 StartY=-25.4373 StartZ=0 EndX=-25 EndY=-25.4373 EndZ=0
    g7: LineSegment StartX=-25 StartY=-25.4373 StartZ=0 EndX=-25 EndY=-48.5 EndZ=0
  constraints (22):
    c: PointOnObject(g4,g-4)
    c: PointOnObject(g0,g-3)
    c: Horizontal(g0)
    c: Coincident(g0,g1)
    c: Coincident(g1,g2)
    c: Vertical(g2)
    c: Coincident(g2,g3)
    c: PointOnObject(g3,g-4)
    c: Coincident(g3,g4)
    c: DistanceX(g0,g0) = 15
    c: Distance(g4,g4) = 35
    c: DistanceY(g2,g2) = 26
    c: Distance(g1,g-1) = 13
    c: Distance(g-2,g2) = 75
    c: Coincident(g0,g5)
    c: Vertical(g5)
    c: Coincident(g5,g6)
    c: Horizontal(g6)
    c: Coincident(g6,g7)
    c: Coincident(g7,g4)
    c: DistanceX(g2,g3) = 15
    c: Vertical(g7)
FEATURE [PartDesign::Pocket] Pocket002
  BaseFeature = -> Pocket001
  Direction = (0,1,-2e-16)
  Length = 5
  Length2 = 5
  Placement = pos=(0,0,0) rot=(1,0,0;1.5708rad)
  Profile = -> Sketch003
  ReferenceAxis = -> Sketch003 [N_Axis]
  Refine = true
  Suppressed = false
  Type = 0
FEATURE [Sketcher::SketchObject] Sketch005
  ArcFitTolerance = 1e-06
  AttachmentSupport = -> [Pocket002]
  ExternalGeometry = -> [Pocket002]
  FullyConstrained = false
  MakeInternals = false
  MapMode = 5
  Placement = pos=(-75,0,0) rot=(0.707107,0,-0.707107;3.14159rad)
  sketch-geometry (5):
    g0: LineSegment StartX=-48.5 StartY=15 StartZ=0 EndX=39 EndY=45 EndZ=0
    g1: LineSegment StartX=39 StartY=45 StartZ=0 EndX=48.5 EndY=45 EndZ=0
    g2: LineSegment StartX=48.5 StartY=45 StartZ=0 EndX=48.5 EndY=7.1e-15 EndZ=0
    g3: LineSegment StartX=48.5 StartY=7.1e-15 StartZ=0 EndX=-48.5 EndY=-1e-14 EndZ=0
    g4: LineSegment StartX=-48.5 StartY=-1e-14 StartZ=0 EndX=-48.5 EndY=15 EndZ=0
  constraints (12):
    c: Coincident(g0,g1)
    c: Coincident(g1,g2)
    c: Coincident(g2,g3)
    c: Coincident(g3,g4)
    c: Coincident(g4,g0)
    c: Vertical(g2)
    c: Horizontal(g1)
    c: DistanceY(g2,g2) = 45
    c: Vertical(g4)
    c: Coincident(g3,g-3)
    c: Coincident(g2,g-4)
    c: Vertical(g0,g-5)
FEATURE [PartDesign::Pad] Pad002
  BaseFeature = -> Pocket002
  Direction = (-1,0,-2e-16)
  Length = 3
  Length2 = 10
  Placement = pos=(0,0,0) rot=(1,0,0;1.5708rad)
  Profile = -> Sketch005
  ReferenceAxis = -> Sketch005 [N_Axis]
  Refine = true
  Suppressed = false
  Type = 0
FEATURE [Sketcher::SketchObject] Sketch006
  ArcFitTolerance = 1e-06
  AttachmentSupport = -> [Pad002]
  ExternalGeometry = -> [Pad002]
  FullyConstrained = false
  MakeInternals = false
  MapMode = 5
  Placement = pos=(-75,0,-2.25e-14) rot=(0.707107,0,0.707107;3.14159rad)
  sketch-geometry (4):
    g0: LineSegment StartX=-48.5 StartY=45 StartZ=0 EndX=-48.5 EndY=15 EndZ=0
    g1: LineSegment StartX=-48.5 StartY=15 StartZ=0 EndX=-39 EndY=15 EndZ=0
    g2: LineSegment StartX=-39 StartY=15 StartZ=0 EndX=-39 EndY=45 EndZ=0
    g3: LineSegment StartX=-39 StartY=45 StartZ=0 EndX=-48.5 EndY=45 EndZ=0
  constraints (9):
    c: Coincident(g0,g1)
    c: Coincident(g1,g2)
    c: Coincident(g2,g3)
    c: Coincident(g3,g0)
    c: Vertical(g0)
    c: Vertical(g2)
    c: Horizontal(g1)
    c: Coincident(g0,g-4)
    c: Coincident(g2,g-4)
FEATURE [PartDesign::Pad] Pad003
  BaseFeature = -> Pad002
  Direction = (1,0,-2e-16)
  Length = 75
  Length2 = 10
  Placement = pos=(0,0,0) rot=(1,0,0;1.5708rad)
  Profile = -> Sketch006
  ReferenceAxis = -> Sketch006 [N_Axis]
  Refine = true
  Suppressed = false
  Type = 0
FEATURE [Sketcher::SketchObject] Sketch007
  ArcFitTolerance = 1e-06
  AttachmentSupport = -> [Pad003]
  FullyConstrained = true
  MakeInternals = false
  MapMode = 5
  Placement = pos=(0,-10,0) rot=(1,0,0;1.5708rad)
  sketch-geometry (3):
    g0: Circle CenterX=-52 CenterY=44 CenterZ=0 NormalX=0 NormalY=0 NormalZ=1 AngleXU=0 Radius=2
    g1: Circle CenterX=-68 CenterY=0 CenterZ=0 NormalX=0 NormalY=0 NormalZ=1 AngleXU=0 Radius=2
    g2: Circle CenterX=-68 CenterY=-18 CenterZ=0 NormalX=0 NormalY=0 NormalZ=1 AngleXU=0 Radius=2
  constraints (9):
    c: Diameter(g0) = 4
    c: Diameter(g1) = 4
    c: PointOnObject(g1,g-1)
    c: Diameter(g2) = 4
    c: DistanceX(g1,g-1) = 68
    c: DistanceX(g2,g-1) = 68
    c: Distance(g2,g-1) = 18
    c: Distance(g0,g-2) = 52
    c: DistanceY(g-1,g0) = 44
FEATURE [PartDesign::Pocket] Pocket003
  BaseFeature = -> Pad003
  Direction = (0,1,-2e-16)
  Length = 8
  Length2 = 5
  Placement = pos=(0,0,0) rot=(1,0,0;1.5708rad)
  Profile = -> Sketch007
  ReferenceAxis = -> Sketch007 [N_Axis]
  Refine = true
  Suppressed = false
  Type = 0
FEATURE [PartDesign::Fillet] Fillet
  Base = -> Pocket003 [Edge57,Edge74,Edge77]
  BaseFeature = -> Pocket003
  Placement = pos=(0,0,0) rot=(1,0,0;1.5708rad)
  Radius = 5
  Refine = true
  SupportTransform = false
  Suppressed = false
  UseAllEdges = false
FEATURE [Sketcher::SketchObject] Sketch008
  ArcFitTolerance = 1e-06
  AttachmentSupport = -> [Fillet]
  FullyConstrained = false
  MakeInternals = false
  MapMode = 5
  Placement = pos=(0,-15,0) rot=(1,0,0;1.5708rad)
  sketch-geometry (4):
    g0: LineSegment StartX=0 StartY=91.9087 StartZ=0 EndX=0 EndY=-58.0986 EndZ=0
    g1: LineSegment StartX=0 StartY=-58.0986 StartZ=0 EndX=97.0826 EndY=-58.0986 EndZ=0
    g2: LineSegment StartX=97.0826 StartY=-58.0986 StartZ=0 EndX=97.0826 EndY=91.9087 EndZ=0
    g3: LineSegment StartX=97.0826 StartY=91.9087 StartZ=0 EndX=0 EndY=91.9087 EndZ=0
  constraints (9):
    c: Coincident(g0,g1)
    c: Coincident(g1,g2)
    c: Coincident(g2,g3)
    c: Coincident(g3,g0)
    c: Vertical(g0)
    c: Vertical(g2)
    c: Horizontal(g1)
    c: Horizontal(g3)
    c: PointOnObject(g0,g-2)
FEATURE [PartDesign::Pocket] Pocket004
  BaseFeature = -> Fillet
  Direction = (0,1,-2e-16)
  Length = 5
  Length2 = 5
  Placement = pos=(0,0,0) rot=(1,0,0;1.5708rad)
  Profile = -> Sketch008
  ReferenceAxis = -> Sketch008 [N_Axis]
  Refine = true
  Suppressed = false
  Type = 1
FEATURE [PartDesign::Mirrored] Mirrored
  BaseFeature = -> Pocket004
  MirrorPlane = -> YZ_Plane
  Placement = pos=(0,0,0) rot=(1,0,0;1.5708rad)
  Refine = true
  Suppressed = false
  TransformMode = 1
FEATURE [Sketcher::SketchObject] Sketch009
  ArcFitTolerance = 1e-06
  AttachmentSupport = -> [Mirrored]
  FullyConstrained = true
  MakeInternals = false
  MapMode = 5
  Placement = pos=(0,9.4e-15,-39) rot=(0,0,1;3.14159rad)
  sketch-geometry (3):
    g0: Circle CenterX=-60 CenterY=38 CenterZ=0 NormalX=0 NormalY=0 NormalZ=1 AngleXU=0 Radius=1.5
    g1: Circle CenterX=0 CenterY=19 CenterZ=0 NormalX=0 NormalY=0 NormalZ=1 AngleXU=0 Radius=1.5
    g2: Circle CenterX=60 CenterY=38 CenterZ=0 NormalX=0 NormalY=0 NormalZ=1 AngleXU=0 Radius=1.5
  constraints (9):
    c: Diameter(g0) = 3
    c: Diameter(g1) = 3
    c: PointOnObject(g1,g-2)
    c: Diameter(g2) = 3
    c: DistanceY(g-1,g0) = 38
    c: DistanceY(g-1,g1) = 19
    c: DistanceX(g-1,g2) = 60
    c: DistanceX(g0,g-1) = 60
    c: Horizontal(g2,g0)
FEATURE [PartDesign::Pocket] Pocket005
  BaseFeature = -> Mirrored
  Direction = (0,0,-1)
  Length = 5
  Length2 = 5
  Placement = pos=(0,0,0) rot=(1,0,0;1.5708rad)
  Profile = -> Sketch009
  ReferenceAxis = -> Sketch009 [N_Axis]
  Refine = true
  Suppressed = false
  Type = 1
FEATURE [Sketcher::SketchObject] Sketch010
  ArcFitTolerance = 1e-06
  AttachmentSupport = -> [XZ_Plane001]
  FullyConstrained = true
  MakeInternals = false
  MapMode = 5
  Placement = pos=(0,0,0) rot=(1,0,0;1.5708rad)
  sketch-geometry (5):
    g0: LineSegment StartX=-60.5 StartY=-38 StartZ=0 EndX=60.5 EndY=-38 EndZ=0
    g1: LineSegment StartX=60.5 StartY=-38 StartZ=0 EndX=60.5 EndY=38 EndZ=0
    g2: LineSegment StartX=60.5 StartY=38 StartZ=0 EndX=-60.5 EndY=38 EndZ=0
    g3: LineSegment StartX=-60.5 StartY=38 StartZ=0 EndX=-60.5 EndY=-38 EndZ=0
    g4: GeomPoint [constr] X=0 Y=0 Z=0
  constraints (12):
    c: Coincident(g0,g1)
    c: Coincident(g1,g2)
    c: Coincident(g2,g3)
    c: Coincident(g3,g0)
    c: Horizontal(g0)
    c: Horizontal(g2)
    c: Vertical(g1)
    c: Vertical(g3)
    c: Symmetric(g2,g0,g4)
    c: Distance(g1,g3) = 121
    c: Distance(g0,g2) = 76
    c: Coincident(g4,g-1)
FEATURE [PartDesign::Pad] Pad004
  Direction = (0,-1,2e-16)
  Length = 3
  Length2 = 10
  Placement = pos=(0,0,0) rot=(1,0,0;1.5708rad)
  Profile = -> Sketch010
  ReferenceAxis = -> Sketch010 [N_Axis]
  Refine = true
  Suppressed = false
  Type = 0
FEATURE [PartDesign::Body] Body001  label="Display"
  AllowCompound = false
  Group = -> [Sketch010,Pad004]
  Origin = -> Origin001
  Placement = pos=(0,-5,0) rot=(0,0,1;0rad)
  Tip = -> Pad004
FEATURE [Sketcher::SketchObject] Sketch011
  ArcFitTolerance = 1e-06
  AttachmentSupport = -> [XZ_Plane002]
  FullyConstrained = false
  MakeInternals = false
  MapMode = 5
  Placement = pos=(0,0,0) rot=(1,0,0;1.5708rad)
  sketch-geometry (9):
    g0: LineSegment StartX=-46 StartY=-27.5 StartZ=0 EndX=46 EndY=-27.5 EndZ=0
    g1: LineSegment StartX=46 StartY=-27.5 StartZ=0 EndX=46 EndY=27.5 EndZ=0
    g2: LineSegment StartX=46 StartY=27.5 StartZ=0 EndX=-46 EndY=27.5 EndZ=0
    g3: LineSegment StartX=-46 StartY=27.5 StartZ=0 EndX=-46 EndY=-27.5 EndZ=0
    g4: GeomPoint [constr] X=0 Y=0 Z=0
    g5: Circle CenterX=-43.5 CenterY=-24.5 CenterZ=0 NormalX=0 NormalY=0 NormalZ=1 AngleXU=0 Radius=1.5
    g6: Circle CenterX=43.5 CenterY=-24.5 CenterZ=0 NormalX=0 NormalY=0 NormalZ=1 AngleXU=0 Radius=1.5
    g7: Circle CenterX=43.5 CenterY=24.5 CenterZ=0 NormalX=0 NormalY=0 NormalZ=1 AngleXU=0 Radius=1.61107
    g8: Circle CenterX=-32.5 CenterY=24.5 CenterZ=0 NormalX=0 NormalY=0 NormalZ=1 AngleXU=0 Radius=1.5
  constraints (23):
    c: Coincident(g0,g1)
    c: Coincident(g1,g2)
    c: Coincident(g2,g3)
    c: Coincident(g3,g0)
    c: Horizontal(g0)
    c: Horizontal(g2)
    c: Vertical(g1)
    c: Vertical(g3)
    c: Symmetric(g2,g0,g4)
    c: Distance(g1,g3) = 92
    c: Distance(g0,g2) = 55
    c: Coincident(g4,g-1)
    c: Diameter(g5) = 3
    c: Diameter(g6) = 3
    c: Diameter(g8) = 3
    c: DistanceX(g-1,g7) = 43.5
    c: Distance(g6,g-2) = 43.5
    c: Distance(g6,g-1) = 24.5
    c: Distance(g5,g-2) = 43.5
    c: Distance(g7,g-1) = 24.5
    c: DistanceY(g-1,g8) = 24.5
    c: Distance(g8,g-2) = 32.5
    c: Distance(g5,g-1) = 24.5
FEATURE [PartDesign::Pad] Pad005
  Direction = (0,-1,2e-16)
  Length = 2
  Length2 = 10
  Placement = pos=(0,0,0) rot=(1,0,0;1.5708rad)
  Profile = -> Sketch011
  ReferenceAxis = -> Sketch011 [N_Axis]
  Refine = true
  Suppressed = false
  Type = 0
FEATURE [Sketcher::SketchObject] Sketch012
  ArcFitTolerance = 1e-06
  AttachmentSupport = -> [Pad005]
  FullyConstrained = false
  MakeInternals = false
  MapMode = 5
  Placement = pos=(0,-2,0) rot=(1,0,0;1.5708rad)
  sketch-geometry (4):
    g0: LineSegment StartX=-12.0469 StartY=34.3473 StartZ=0 EndX=-12.0469 EndY=18.9109 EndZ=0
    g1: LineSegment StartX=-12.0469 StartY=18.9109 StartZ=0 EndX=14.5809 EndY=18.9109 EndZ=0
    g2: LineSegment StartX=14.5809 StartY=18.9109 StartZ=0 EndX=14.5809 EndY=34.3473 EndZ=0
    g3: LineSegment StartX=14.5809 StartY=34.3473 StartZ=0 EndX=-12.0469 EndY=34.3473 EndZ=0
  constraints (8):
    c: Coincident(g0,g1)
    c: Coincident(g1,g2)
    c: Coincident(g2,g3)
    c: Coincident(g3,g0)
    c: Vertical(g0)
    c: Vertical(g2)
    c: Horizontal(g1)
    c: Horizontal(g3)
FEATURE [PartDesign::Pad] Pad006
  BaseFeature = -> Pad005
  Direction = (0,-1,2e-16)
  Length = 10
  Length2 = 10
  Placement = pos=(0,0,0) rot=(1,0,0;1.5708rad)
  Profile = -> Sketch012
  ReferenceAxis = -> Sketch012 [N_Axis]
  Refine = true
  Suppressed = false
  Type = 0
FEATURE [PartDesign::Body] Body002  label="HDMIBridge"
  AllowCompound = false
  Group = -> [Sketch011,Pad005,Sketch012,Pad006]
  Origin = -> Origin002
  Placement = pos=(0,-15.5,-5.6) rot=(0,0,1;0rad)
  Tip = -> Pad006
FEATURE [Sketcher::SketchObject] Sketch013
  ArcFitTolerance = 1e-06
  AttachmentSupport = -> [XZ_Plane003]
  FullyConstrained = false
  MakeInternals = false
  MapMode = 5
  Placement = pos=(0,0,0) rot=(1,0,0;1.5708rad)
  sketch-geometry (33):
    g0: LineSegment StartX=-60 StartY=48.5 StartZ=0 EndX=-46 EndY=48.5 EndZ=0
    g1: LineSegment StartX=-46 StartY=48.5 StartZ=0 EndX=-46 EndY=31.2652 EndZ=0
    g2: LineSegment StartX=-46 StartY=31.2652 StartZ=0 EndX=-42.9656 EndY=28.2308 EndZ=0
    g3: LineSegment StartX=-42.9656 StartY=28.2308 StartZ=0 EndX=41.8391 EndY=28.2308 EndZ=0
    g4: LineSegment StartX=41.8391 StartY=28.2308 StartZ=0 EndX=46 EndY=32.3918 EndZ=0
    g5: LineSegment StartX=46 StartY=32.3918 StartZ=0 EndX=46 EndY=48.5 EndZ=0
    g6: LineSegment StartX=46 StartY=48.5 StartZ=0 EndX=60 EndY=48.5 EndZ=0
    g7: LineSegment StartX=60 StartY=48.5 StartZ=0 EndX=75 EndY=13 EndZ=0
    g8: LineSegment StartX=75 StartY=13 StartZ=0 EndX=75 EndY=-13 EndZ=0
    g9: LineSegment StartX=75 StartY=-13 StartZ=0 EndX=60 EndY=-48.5 EndZ=0
    g10: LineSegment StartX=60 StartY=-48.5 StartZ=0 EndX=40 EndY=-48.5 EndZ=0
    g11: LineSegment StartX=40 StartY=-48.5 StartZ=0 EndX=40 EndY=-38 EndZ=0
    g12: LineSegment StartX=40 StartY=-38 StartZ=0 EndX=-26 EndY=-38 EndZ=0
    g13: LineSegment StartX=-26 StartY=-38 StartZ=0 EndX=-26 EndY=-48.5 EndZ=0
    g14: LineSegment StartX=-26 StartY=-48.5 StartZ=0 EndX=-60 EndY=-48.5 EndZ=0
    g15: LineSegment StartX=-60 StartY=-48.5 StartZ=0 EndX=-75 EndY=-13 EndZ=0
    g16: LineSegment StartX=-75 StartY=-13 StartZ=0 EndX=-75 EndY=13 EndZ=0
    g17: LineSegment StartX=-75 StartY=13 StartZ=0 EndX=-60 EndY=48.5 EndZ=0
    g18: Circle CenterX=-52 CenterY=44 CenterZ=0 NormalX=0 NormalY=0 NormalZ=1 AngleXU=0 Radius=1.5
    g19: Circle CenterX=-68 CenterY=0 CenterZ=0 NormalX=0 NormalY=0 NormalZ=1 AngleXU=0 Radius=1.5
    g20: Circle CenterX=-68 CenterY=-18 CenterZ=0 NormalX=0 NormalY=0 NormalZ=1 AngleXU=0 Radius=1.5
    g21: Circle CenterX=52 CenterY=44 CenterZ=0 NormalX=0 NormalY=0 NormalZ=1 AngleXU=0 Radius=1.5
    g22: Circle CenterX=68 CenterY=0 CenterZ=0 NormalX=0 NormalY=0 NormalZ=1 AngleXU=0 Radius=1.5
    g23: Circle CenterX=68 CenterY=-18 CenterZ=0 NormalX=0 NormalY=0 NormalZ=1 AngleXU=0 Radius=1.5
    g24: LineSegment StartX=55 StartY=-23.6617 StartZ=0 EndX=55 EndY=14.2073 EndZ=0
    g25: LineSegment StartX=55 StartY=14.2073 StartZ=0 EndX=-55 EndY=14.2073 EndZ=0
    g26: LineSegment StartX=-55 StartY=14.2073 StartZ=0 EndX=-55 EndY=-23.6617 EndZ=0
    g27: LineSegment StartX=-55 StartY=-23.6617 StartZ=0 EndX=55 EndY=-23.6617 EndZ=0
    g28: GeomPoint [constr] X=0 Y=0 Z=0
    g29: Circle CenterX=-27 CenterY=17.963 CenterZ=0 NormalX=0 NormalY=0 NormalZ=1 AngleXU=0 Radius=1.5
    g30: Circle CenterX=44.5 CenterY=17.963 CenterZ=0 NormalX=0 NormalY=0 NormalZ=1 AngleXU=0 Radius=1.5
    g31: Circle CenterX=-37 CenterY=-28.037 CenterZ=0 NormalX=0 NormalY=0 NormalZ=1 AngleXU=0 Radius=1.5
    g32: Circle CenterX=45.5 CenterY=-28.037 CenterZ=0 NormalX=0 NormalY=0 NormalZ=1 AngleXU=0 Radius=1.5
  constraints (91):
    c: Horizontal(g0)
    c: Coincident(g0,g1)
    c: Vertical(g1)
    c: Coincident(g1,g2)
    c: Coincident(g2,g3)
    c: Horizontal(g3)
    c: Coincident(g3,g4)
    c: Coincident(g4,g5)
    c: Vertical(g5)
    c: Coincident(g5,g6)
    c: Horizontal(g6)
    c: Coincident(g6,g7)
    c: Coincident(g7,g8)
    c: Vertical(g8)
    c: Coincident(g8,g9)
    c: Horizontal(g10)
    c: Coincident(g10,g11)
    c: Vertical(g11)
    c: Coincident(g11,g12)
    c: Horizontal(g12)
    c: Coincident(g12,g13)
    c: Vertical(g13)
    c: Coincident(g13,g14)
    c: Horizontal(g14)
    c: Coincident(g14,g15)
    c: Coincident(g15,g16)
    c: Vertical(g16)
    c: Coincident(g16,g17)
    c: Coincident(g17,g0)
    c: Coincident(g9,g10)
    c: DistanceX(g0,g-1) = 60
    c: DistanceX(g0,g-1) = 46
    c: Distance(g-1,g0) = 48.5
    c: Angle(g3,g2) = 2.35619
    c: Angle(g4,g3) = 2.35619
    c: DistanceX(g-1,g5) = 46
    c: DistanceX(g-1,g6) = 60
    c: Distance(g-1,g6) = 48.5
    c: DistanceX(g16,g-1) = 75
    c: Distance(g16,g-1) = 13
    c: Distance(g15,g-1) = 13
    c: DistanceX(g14,g-1) = 60
    c: Distance(g-2,g13) = 26
    c: Distance(g-2,g11) = 40
    c: DistanceY(g13,g13) = 10.5
    c: Distance(g11,g11) = 10.5
    c: Distance(g-1,g12) = 38
    c: DistanceX(g-1,g9) = 60
    c: Distance(g-2,g8) = 75
    c: Distance(g7,g-1) = 13
    c: DistanceY(g8,g-1) = 13
    c: Diameter(g18) = 3
    c: Diameter(g19) = 3
    c: PointOnObject(g19,g-1)
    c: PointOnObject(g22,g-1)
    c: DistanceX(g18,g-1) = 52
    c: Distance(g18,g-1) = 44
    c: DistanceX(g19,g-1) = 68
    c: Distance(g20,g-2) = 68
    c: DistanceY(g20,g-1) = 18
    c: Diameter(g20) = 3
    c: Diameter(g21) = 3
    c: Distance(g21,g-2) = 52
    c: Distance(g21,g-1) = 44
    c: Diameter(g22) = 3
    c: DistanceX(g-1,g22) = 68
    c: Diameter(g23) = 3
    c: DistanceY(g23,g-1) = 18
    c: Distance(g23,g-2) = 68
    c: Coincident(g24,g25)
    c: Coincident(g25,g26)
    c: Coincident(g26,g27)
    c: Coincident(g27,g24)
    c: Vertical(g24)
    c: Vertical(g26)
    c: Horizontal(g25)
    c: Horizontal(g27)
    c: Coincident(g28,g-1)
    c: Diameter(g29) = 3
    c: Diameter(g30) = 3
    c: Diameter(g31) = 3
    c: Diameter(g32) = 3
    c: Distance(g32,g-2) = 45.5
    c: DistanceX(g31,g32) = 82.5
    c: DistanceX(g-1,g30) = 44.5
    c: DistanceY(g32,g30) = 46
    c: Horizontal(g31,g32)
    c: Horizontal(g29,g30)
    c: DistanceX(g29,g30) = 71.5
    c: Distance(g-2,g26) = 55
    c: Distance(g-2,g24) = 55
FEATURE [PartDesign::Pad] Pad007
  Direction = (0,-1,2e-16)
  Length = 3
  Length2 = 10
  Placement = pos=(0,0,0) rot=(1,0,0;1.5708rad)
  Profile = -> Sketch013
  ReferenceAxis = -> Sketch013 [N_Axis]
  Refine = true
  Suppressed = false
  Type = 0
FEATURE [PartDesign::Body] Body003  label="DisplayLid"
  AllowCompound = false
  Group = -> [Sketch013,Pad007]
  Origin = -> Origin003
  Placement = pos=(0,-10,0) rot=(0,0,1;0rad)
  Tip = -> Pad007
FEATURE [PartDesign::Hole] Hole
  BaseFeature = -> Pocket005
  CustomThreadClearance = 0
  Depth = 5
  DepthType = 0
  Diameter = 8
  DrillForDepth = false
  DrillPoint = 1
  DrillPointAngle = 118
  HoleCutCountersinkAngle = 90
  HoleCutCustomValues = false
  HoleCutDepth = 0
  HoleCutDiameter = 6.1
  HoleCutType = 0
  ModelThread = false
  Placement = pos=(0,0,0) rot=(1,0,0;1.5708rad)
  Profile = -> Pocket005 [Edge66,Edge65,Edge67]
  Refine = true
  Suppressed = false
  Tapered = false
  TaperedAngle = 90
  ThreadClass = 0
  ThreadDepth = 5
  ThreadDepthType = 0
  ThreadDirection = 0
  ThreadFit = 0
  ThreadSize = 0
  ThreadType = 0
  Threaded = false
  UseCustomThreadClearance = false
FEATURE [PartDesign::Fillet] Fillet001
  Base = -> Hole [Edge148,Edge145,Edge147,Edge146]
  BaseFeature = -> Hole
  Placement = pos=(0,0,0) rot=(1,0,0;1.5708rad)
  Radius = 10
  Refine = true
  SupportTransform = false
  Suppressed = false
  UseAllEdges = false
FEATURE [PartDesign::Body] Body  label="MainDisplay"
  AllowCompound = false
  Group = -> [Sketch,Pad,Sketch001,Pocket,Sketch002,Pocket001,Sketch003,Pocket002,Sketch005,Pad002,Sketch006,Pad003,Sketch007,Pocket003,Fillet,Sketch008,Pocket004,Mirrored,Sketch009,Pocket005,Hole,Fillet001]
  Origin = -> Origin
  Tip = -> Fillet001
FEATURE [App::LinkGroup] LinkGroup  label="DisplayGroup"
  ElementList = -> [Body,Body001,Body002,Body003]
  LinkMode = 0
---- part GT2_80.FCStd = doc fcstd_a1a16ebba8dd (164286 chars; too large to inline — full recipe in that document) ----
---- part RobotBody.FCStd = doc fcstd_933c1abd92ae (70074 chars; too large to inline — full recipe in that document) ----
